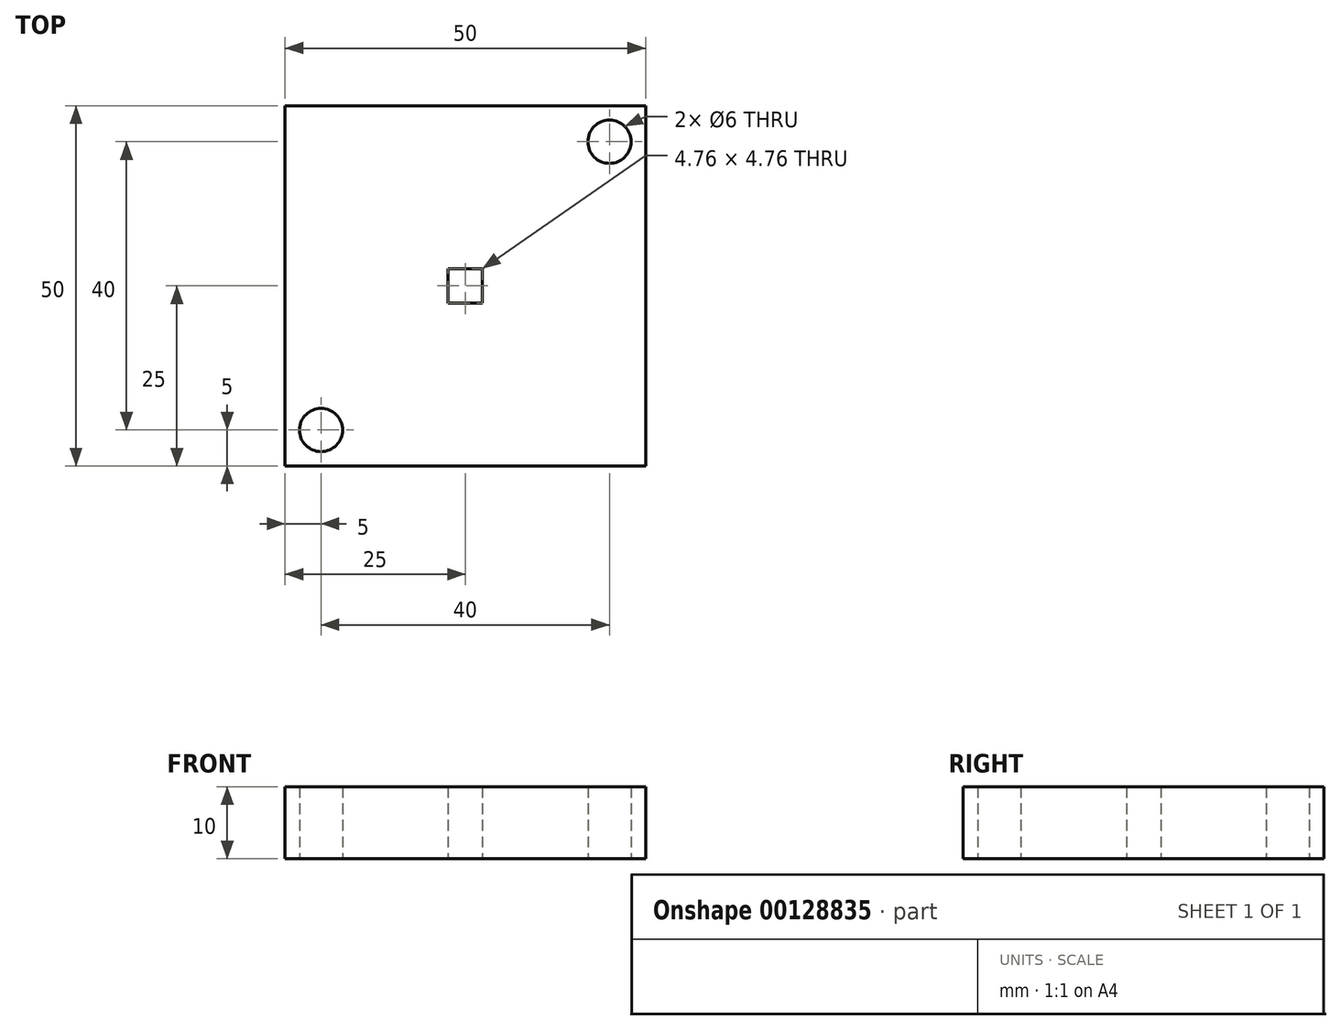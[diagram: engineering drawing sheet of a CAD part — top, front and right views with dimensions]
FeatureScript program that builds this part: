
annotation { "Feature Type Name" : "Feature", "Feature Type Description" : "" }
export const myFeature = defineFeature(function(context is Context, id is Id, definition is map)
    precondition{}
    {
        {
            var Q0;
            Q0=qCreatedBy(makeId("Top.planeOp"),FACE);
            var sketch = newSketch(context, id + "F0", { "sketchPlane" : qUnion([Q0])});
            skLineSegment(sketch, "E0.bottom", {"start": v(0, 0) * mm, "end": v(50, 0) * mm});
            skLineSegment(sketch, "E0.top", {"start": v(0, -50) * mm, "end": v(50, -50) * mm});
            skLineSegment(sketch, "E0.left", {"start": v(0, 0) * mm, "end": v(0, -50) * mm});
            skLineSegment(sketch, "E0.right", {"start": v(50, 0) * mm, "end": v(50, -50) * mm});
            skLineSegment(sketch, "E1", {"start": v(25, 0) * mm, "end": v(25, -50) * mm, "construction": true});
            skLineSegment(sketch, "E2", {"start": v(0, -25) * mm, "end": v(50, -25) * mm, "construction": true});
            skLineSegment(sketch, "E3.bottom", {"start": v(27.38, -27.38) * mm, "end": v(22.62, -27.38) * mm});
            skLineSegment(sketch, "E3.top", {"start": v(27.38, -22.62) * mm, "end": v(22.62, -22.62) * mm});
            skLineSegment(sketch, "E3.left", {"start": v(27.38, -27.38) * mm, "end": v(27.38, -22.62) * mm});
            skLineSegment(sketch, "E3.right", {"start": v(22.62, -27.38) * mm, "end": v(22.62, -22.62) * mm});
            skPoint(sketch, "E3.middle", {"position": v(25, -25) * mm});
            skCircle(sketch, "E4", {"center": v(5, -45) * mm, "radius": 3 * mm});
            skCircle(sketch, "E5", {"center": v(45, -5) * mm, "radius": 3 * mm});
            skSolve(sketch);
        }
        {
            var Q0;
            Q0=makeQuery(id+"F0.imprint","IMPRINT",FACE,{"disambiguationData":[TD([[makeQuery(id+"F0.imprint","IMPRINT",EDGE,{"derivedFrom":sQuery(id+"F0.wireOp",EDGE,"E0.bottom")}),-1.0]])]});
            extrude(context, id + "F1", {"entities" : qUnion([Q0]), "depth" : 10 * mm});
        }
    });
